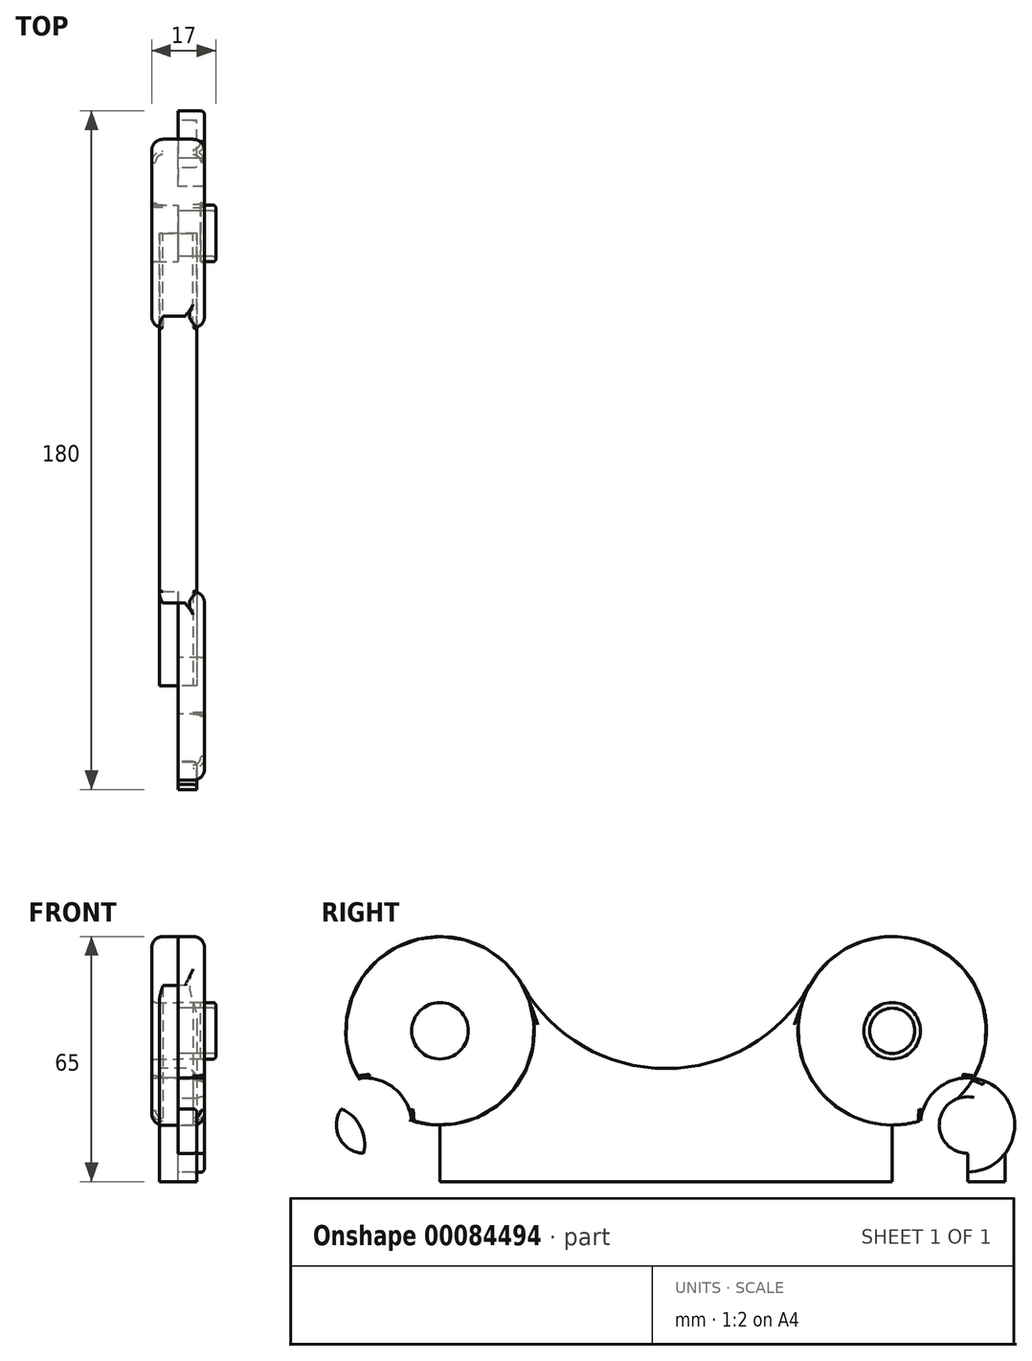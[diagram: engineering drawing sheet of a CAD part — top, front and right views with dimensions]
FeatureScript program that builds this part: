
annotation { "Feature Type Name" : "Feature", "Feature Type Description" : "" }
export const myFeature = defineFeature(function(context is Context, id is Id, definition is map)
    precondition{}
    {
        {
            var Q0;
            Q0=qCreatedBy(makeId("Right.planeOp"),FACE);
            var sketch = newSketch(context, id + "F0", { "sketchPlane" : qUnion([Q0])});
            skLineSegment(sketch, "E0.bottom", {"start": v(30, -20) * mm, "end": v(-30, -20) * mm});
            skLineSegment(sketch, "E0.top", {"start": v(30, 20) * mm, "end": v(-30, 20) * mm});
            skLineSegment(sketch, "E0.left", {"start": v(30, -20) * mm, "end": v(30, 20) * mm});
            skLineSegment(sketch, "E0.right", {"start": v(-30, -20) * mm, "end": v(-30, 20) * mm});
            skPoint(sketch, "E0.middle", {"position": v(0, 0) * mm});
            skCircle(sketch, "E1", {"center": v(30, 20) * mm, "radius": 25 * mm});
            skArc(sketch, "E2", {"start": v(-30, 10) * mm, "mid": v(-7.87, 15.98) * mm, "end": v(8.24, 32.3) * mm});
            skLineSegment(sketch, "E3", {"start": v(30, -20) * mm, "end": v(70, -20) * mm});
            skLineSegment(sketch, "E4", {"start": v(70, -20) * mm, "end": v(60, -20) * mm});
            skLineSegment(sketch, "E5", {"start": v(60, -20) * mm, "end": v(60, -10) * mm});
            skCircle(sketch, "E6", {"center": v(60, -10) * mm, "radius": 10 * mm});
            skLineSegment(sketch, "E7", {"start": v(69.11, -5.89) * mm, "end": v(52.79, 30.29) * mm});
            skLineSegment(sketch, "E8", {"start": v(60, -20) * mm, "end": v(50, -20) * mm});
            skLineSegment(sketch, "E9", {"start": v(50, -20) * mm, "end": v(50, -5) * mm});
            skCircle(sketch, "E10", {"center": v(50, -5) * mm, "radius": 7.5 * mm});
            skCircle(sketch, "E11.cCircle", {"center": v(50, -5) * mm, "radius": 7.5 * mm, "construction": true});
            skCircle(sketch, "E12", {"center": v(30, 20) * mm, "radius": 7.5 * mm});
            skCircle(sketch, "E13.cCircle", {"center": v(30, 20) * mm, "radius": 7.5 * mm, "construction": true});
            skCircle(sketch, "E14", {"center": v(50, -5) * mm, "radius": 12.5 * mm});
            skLineSegment(sketch, "E15", {"start": v(-30, 10) * mm, "end": v(30, 10) * mm});
            skCircle(sketch, "E16", {"center": v(30, 20) * mm, "radius": 6 * mm});
            skSolve(sketch);
        }
        {
            var Q0;
            {var subQ1=sQuery(id+"F0.wireOp",EDGE,"E0.bottom");Q0=makeQuery(id+"F0.imprint","IMPRINT",FACE,{"disambiguationData":[TD([[makeQuery(id+"F0.imprint","IMPRINT",EDGE,{"derivedFrom":subQ1}),-1.0]])]});}
            var Q1;
            {var subQ0=sQuery(id+"F0.wireOp",EDGE,"E13.2");Q1=makeQuery(id+"F0.imprint","IMPRINT",FACE,{"disambiguationData":[TD([[makeQuery(id+"F0.imprint","IMPRINT",EDGE,{"derivedFrom":subQ0}),-1.0]])]});}
            var Q2;
            {var subQ5=sQuery(id+"F0.wireOp",EDGE,"E13.0");Q2=makeQuery(id+"F0.imprint","IMPRINT",FACE,{"disambiguationData":[TD([[makeQuery(id+"F0.imprint","IMPRINT",EDGE,{"derivedFrom":subQ5}),-1.0]])]});}
            var Q3;
            {var subQ5=sQuery(id+"F0.wireOp",EDGE,"9949395a-d663-43b6-ab1f-91bd425a46a5.5");Q3=makeQuery(id+"F0.imprint","IMPRINT",FACE,{"disambiguationData":[TD([[makeQuery(id+"F0.imprint","IMPRINT",EDGE,{"derivedFrom":subQ5}),-1.0]])]});}
            var Q4;
            {var subQ3=sQuery(id+"F0.wireOp",EDGE,"9949395a-d663-43b6-ab1f-91bd425a46a5.0");Q4=makeQuery(id+"F0.imprint","IMPRINT",FACE,{"disambiguationData":[TD([[makeQuery(id+"F0.imprint","IMPRINT",EDGE,{"derivedFrom":subQ3}),-1.0]])]});}
            var Q5;
            {var subQ7=sQuery(id+"F0.wireOp",EDGE,"E3");Q5=makeQuery(id+"F0.imprint","IMPRINT",FACE,{"disambiguationData":[TD([[makeQuery(id+"F0.imprint","IMPRINT",EDGE,{"derivedFrom":subQ7}),1.0]])]});}
            var Q6;
            {var subQ7=sQuery(id+"F0.wireOp",EDGE,"RmBogFvs-hSfI-Fk4R-dt5A-n03ufGh0CfcG");Q6=makeQuery(id+"F0.imprint","IMPRINT",FACE,{"disambiguationData":[TD([[makeQuery(id+"F0.imprint","IMPRINT",EDGE,{"derivedFrom":subQ7}),-1.0]])]});}
            var Q7;
            {var subQ0=sQuery(id+"F0.wireOp",EDGE,"2t1OXQJq-y7Vc-evad-L2Xn-u0VWQIfUzRHt");var subQ1=makeQuery(id+"F0.imprint","INTERSECT",VERTEX,{"derivedFrom":[subQ0,sQuery(id+"F0.wireOp",EDGE,"sKefAVml-Ko5n-3xTP-831O-t11bm8OxiufM")]});Q7=makeQuery(id+"F0.imprint","IMPRINT",FACE,{"disambiguationData":[TD([[makeQuery(id+"F0.imprint","IMPRINT",EDGE,{"disambiguationData":[TD([[subQ1,1.0]])],"derivedFrom":subQ0}),1.0]])]});}
            var Q8;
            {var subQ5=sQuery(id+"F0.wireOp",EDGE,"bd8dee19-a407-44eb-8f93-f0fc487aa449.3");Q8=makeQuery(id+"F0.imprint","IMPRINT",FACE,{"disambiguationData":[TD([[makeQuery(id+"F0.imprint","IMPRINT",EDGE,{"derivedFrom":subQ5}),-1.0]])]});}
            var Q9;
            {var subQ0=sQuery(id+"F0.wireOp",EDGE,"bd8dee19-a407-44eb-8f93-f0fc487aa449.1");Q9=makeQuery(id+"F0.imprint","IMPRINT",FACE,{"disambiguationData":[TD([[makeQuery(id+"F0.imprint","IMPRINT",EDGE,{"derivedFrom":subQ0}),-1.0]])]});}
            var Q10;
            {var subQ0=sQuery(id+"F0.wireOp",EDGE,"E11.0");Q10=makeQuery(id+"F0.imprint","IMPRINT",FACE,{"disambiguationData":[TD([[makeQuery(id+"F0.imprint","IMPRINT",EDGE,{"derivedFrom":subQ0}),-1.0]])]});}
            var Q11;
            {var subQ0=sQuery(id+"F0.wireOp",EDGE,"E11.4");Q11=makeQuery(id+"F0.imprint","IMPRINT",FACE,{"disambiguationData":[TD([[makeQuery(id+"F0.imprint","IMPRINT",EDGE,{"derivedFrom":subQ0}),-1.0]])]});}
            var Q12;
            {var subQ0=sQuery(id+"F0.wireOp",EDGE,"46ax8Qey-YlKV-k2xy-i6VS-7Ej97oajGADz");var subQ1=sQuery(id+"F0.wireOp",EDGE,"2t1OXQJq-y7Vc-evad-L2Xn-u0VWQIfUzRHt");var subQ2=makeQuery(id+"F0.imprint","INTERSECT",VERTEX,{"derivedFrom":[subQ1,subQ0]});Q12=makeQuery(id+"F0.imprint","IMPRINT",FACE,{"disambiguationData":[TD([[makeQuery(id+"F0.imprint","IMPRINT",EDGE,{"disambiguationData":[TD([[subQ2,1.0]])],"derivedFrom":subQ1}),-1.0]])]});}
            var Q13;
            {var subQ0=sQuery(id+"F0.wireOp",EDGE,"3qyVSIB1-lFnq-SXgv-lqWt-4zmXsfzFFz89");Q13=makeQuery(id+"F0.imprint","IMPRINT",FACE,{"disambiguationData":[TD([[makeQuery(id+"F0.imprint","IMPRINT",EDGE,{"derivedFrom":subQ0}),1.0]])]});}
            var Q14;
            {var subQ0=sQuery(id+"F0.wireOp",EDGE,"E2");var subQ1=sQuery(id+"F0.wireOp",EDGE,"E0.top");var subQ2=makeQuery(id+"F0.imprint","INTERSECT",VERTEX,{"disambiguationData":[OD(1.0)],"derivedFrom":[subQ1,subQ0]});Q14=makeQuery(id+"F0.imprint","IMPRINT",FACE,{"disambiguationData":[TD([[makeQuery(id+"F0.imprint","IMPRINT",EDGE,{"disambiguationData":[TD([[subQ2,-1.0]])],"derivedFrom":subQ1}),-1.0]])]});}
            var Q15;
            {var subQ0=sQuery(id+"F0.wireOp",EDGE,"E2");var subQ1=sQuery(id+"F0.wireOp",EDGE,"E0.top");var subQ2=makeQuery(id+"F0.imprint","INTERSECT",VERTEX,{"disambiguationData":[OD(0.0)],"derivedFrom":[subQ1,subQ0]});Q15=makeQuery(id+"F0.imprint","IMPRINT",FACE,{"disambiguationData":[TD([[makeQuery(id+"F0.imprint","IMPRINT",EDGE,{"disambiguationData":[TD([[subQ2,1.0]])],"derivedFrom":subQ1}),-1.0]])]});}
            var Q16;
            {var subQ0=sQuery(id+"F0.wireOp",EDGE,"E6");var subQ1=makeQuery(id+"F0.imprint","INTERSECT",VERTEX,{"derivedFrom":[subQ0,sQuery(id+"F0.wireOp",EDGE,"E7")]});Q16=makeQuery(id+"F0.imprint","IMPRINT",FACE,{"disambiguationData":[TD([[makeQuery(id+"F0.imprint","IMPRINT",EDGE,{"disambiguationData":[TD([[subQ1,-1.0]])],"derivedFrom":subQ0}),1.0]])]});}
            var Q17;
            {var subQ0=sQuery(id+"F0.wireOp",EDGE,"E8");Q17=makeQuery(id+"F0.imprint","IMPRINT",FACE,{"disambiguationData":[TD([[makeQuery(id+"F0.imprint","IMPRINT",EDGE,{"derivedFrom":subQ0}),-1.0]])]});}
            var Q18;
            {var subQ0=sQuery(id+"F0.wireOp",EDGE,"E2");var subQ1=sQuery(id+"F0.wireOp",EDGE,"E0.top");var subQ2=makeQuery(id+"F0.imprint","INTERSECT",VERTEX,{"derivedFrom":[subQ1,subQ0]});Q18=makeQuery(id+"F0.imprint","IMPRINT",FACE,{"disambiguationData":[TD([[makeQuery(id+"F0.imprint","IMPRINT",EDGE,{"disambiguationData":[TD([[subQ2,1.0]])],"derivedFrom":subQ1}),1.0]])]});}
            var Q19;
            {var subQ1=sQuery(id+"F0.wireOp",EDGE,"E5");var subQ3=sQuery(id+"F0.wireOp",EDGE,"E14");var subQ4=makeQuery(id+"F0.imprint","INTERSECT",VERTEX,{"derivedFrom":[subQ1,subQ3]});Q19=makeQuery(id+"F0.imprint","IMPRINT",FACE,{"disambiguationData":[TD([[makeQuery(id+"F0.imprint","IMPRINT",EDGE,{"disambiguationData":[TD([[subQ4,1.0]])],"derivedFrom":subQ3}),-1.0]])]});}
            var Q20;
            {var subQ0=sQuery(id+"F0.wireOp",EDGE,"E7");Q20=makeQuery(id+"F0.imprint","IMPRINT",FACE,{"disambiguationData":[TD([[makeQuery(id+"F0.imprint","IMPRINT",EDGE,{"derivedFrom":subQ0}),1.0]])]});}
            extrude(context, id + "F1", {"entities" : qUnion([Q0, Q1, Q2, Q3, Q4, Q5, Q6, Q7, Q8, Q9, Q10, Q11, Q12, Q13, Q14, Q15, Q16, Q17, Q18, Q19, Q20]), "depth" : 5 * mm});
        }
        {
            var Q0;
            {var subQ5=sQuery(id+"F0.wireOp",EDGE,"E12");var subQ8=sQuery(id+"F0.wireOp",EDGE,"E0.top");var subQ9=makeQuery(id+"F0.imprint","INTERSECT",VERTEX,{"derivedFrom":[subQ8,subQ5]});Q0=makeQuery(id+"F0.imprint","IMPRINT",FACE,{"disambiguationData":[TD([[makeQuery(id+"F0.imprint","IMPRINT",EDGE,{"disambiguationData":[TD([[subQ9,-1.0]])],"derivedFrom":subQ8}),-1.0]])]});}
            var Q1;
            {var subQ1=sQuery(id+"F0.wireOp",EDGE,"E0.top");var subQ5=sQuery(id+"F0.wireOp",EDGE,"E12");var subQ6=makeQuery(id+"F0.imprint","INTERSECT",VERTEX,{"derivedFrom":[subQ1,subQ5]});Q1=makeQuery(id+"F0.imprint","IMPRINT",FACE,{"disambiguationData":[TD([[makeQuery(id+"F0.imprint","IMPRINT",EDGE,{"disambiguationData":[TD([[subQ6,-1.0]])],"derivedFrom":subQ1}),1.0]])]});}
            var Q2;
            {var subQ0=sQuery(id+"F0.wireOp",EDGE,"E15");var subQ1=sQuery(id+"F0.wireOp",EDGE,"E0.left");var subQ2=makeQuery(id+"F0.imprint","INTERSECT",VERTEX,{"derivedFrom":[subQ1,subQ0]});Q2=makeQuery(id+"F0.imprint","IMPRINT",FACE,{"disambiguationData":[TD([[makeQuery(id+"F0.imprint","IMPRINT",EDGE,{"disambiguationData":[TD([[subQ2,1.0]])],"derivedFrom":subQ1}),1.0]])]});}
            var Q3;
            {var subQ0=sQuery(id+"F0.wireOp",EDGE,"E14");var subQ1=sQuery(id+"F0.wireOp",EDGE,"E6");var subQ2=makeQuery(id+"F0.imprint","INTERSECT",VERTEX,{"disambiguationData":[OD(0.0)],"derivedFrom":[subQ1,subQ0]});Q3=makeQuery(id+"F0.imprint","IMPRINT",FACE,{"disambiguationData":[TD([[makeQuery(id+"F0.imprint","IMPRINT",EDGE,{"disambiguationData":[TD([[subQ2,-1.0]])],"derivedFrom":subQ1}),-1.0]])]});}
            var Q4;
            {var subQ0=sQuery(id+"F0.wireOp",EDGE,"E14");var subQ2=sQuery(id+"F0.wireOp",EDGE,"E6");var subQ7=makeQuery(id+"F0.imprint","INTERSECT",VERTEX,{"disambiguationData":[OD(0.0)],"derivedFrom":[subQ2,subQ0]});Q4=makeQuery(id+"F0.imprint","IMPRINT",FACE,{"disambiguationData":[TD([[makeQuery(id+"F0.imprint","IMPRINT",EDGE,{"disambiguationData":[TD([[subQ7,-1.0]])],"derivedFrom":subQ2}),1.0]])]});}
            var Q5;
            {var subQ0=sQuery(id+"F0.wireOp",EDGE,"E10");var subQ1=sQuery(id+"F0.wireOp",EDGE,"E6");var subQ2=makeQuery(id+"F0.imprint","INTERSECT",VERTEX,{"disambiguationData":[OD(1.0)],"derivedFrom":[subQ1,subQ0]});Q5=makeQuery(id+"F0.imprint","IMPRINT",FACE,{"disambiguationData":[TD([[makeQuery(id+"F0.imprint","IMPRINT",EDGE,{"disambiguationData":[TD([[subQ2,-1.0]])],"derivedFrom":subQ1}),-1.0]])]});}
            var Q6;
            {var subQ0=sQuery(id+"F0.wireOp",EDGE,"E14");var subQ1=sQuery(id+"F0.wireOp",EDGE,"E1");var subQ2=makeQuery(id+"F0.imprint","INTERSECT",VERTEX,{"disambiguationData":[OD(0.0)],"derivedFrom":[subQ1,subQ0]});Q6=makeQuery(id+"F0.imprint","IMPRINT",FACE,{"disambiguationData":[TD([[makeQuery(id+"F0.imprint","IMPRINT",EDGE,{"disambiguationData":[TD([[subQ2,-1.0]])],"derivedFrom":subQ1}),1.0]])]});}
            var Q7;
            {var subQ0=sQuery(id+"F0.wireOp",EDGE,"E14");var subQ1=sQuery(id+"F0.wireOp",EDGE,"E1");var subQ2=makeQuery(id+"F0.imprint","INTERSECT",VERTEX,{"disambiguationData":[OD(0.0)],"derivedFrom":[subQ1,subQ0]});Q7=makeQuery(id+"F0.imprint","IMPRINT",FACE,{"disambiguationData":[TD([[makeQuery(id+"F0.imprint","IMPRINT",EDGE,{"disambiguationData":[TD([[subQ2,-1.0]])],"derivedFrom":subQ1}),-1.0]])]});}
            var Q8;
            {var subQ0=sQuery(id+"F0.wireOp",EDGE,"E0.left");var subQ1=sQuery(id+"F0.wireOp",EDGE,"E0.top");var subQ2=makeQuery(id+"F0.imprint","INTERSECT",VERTEX,{"derivedFrom":[subQ1,subQ0]});Q8=makeQuery(id+"F0.imprint","IMPRINT",FACE,{"disambiguationData":[TD([[makeQuery(id+"F0.imprint","IMPRINT",EDGE,{"disambiguationData":[TD([[subQ2,-1.0]])],"derivedFrom":subQ1}),1.0]])]});}
            var Q9;
            {var subQ0=sQuery(id+"F0.wireOp",EDGE,"E0.left");var subQ1=sQuery(id+"F0.wireOp",EDGE,"E0.top");var subQ2=makeQuery(id+"F0.imprint","INTERSECT",VERTEX,{"derivedFrom":[subQ1,subQ0]});Q9=makeQuery(id+"F0.imprint","IMPRINT",FACE,{"disambiguationData":[TD([[makeQuery(id+"F0.imprint","IMPRINT",EDGE,{"disambiguationData":[TD([[subQ2,-1.0]])],"derivedFrom":subQ1}),-1.0]])]});}
            var Q10;
            {var subQ0=sQuery(id+"F0.wireOp",EDGE,"E10");var subQ1=sQuery(id+"F0.wireOp",EDGE,"E1");var subQ2=makeQuery(id+"F0.imprint","INTERSECT",VERTEX,{"disambiguationData":[OD(0.0)],"derivedFrom":[subQ1,subQ0]});Q10=makeQuery(id+"F0.imprint","IMPRINT",FACE,{"disambiguationData":[TD([[makeQuery(id+"F0.imprint","IMPRINT",EDGE,{"disambiguationData":[TD([[subQ2,-1.0]])],"derivedFrom":subQ1}),1.0]])]});}
            var Q11;
            {var subQ0=sQuery(id+"F0.wireOp",EDGE,"E10");var subQ1=sQuery(id+"F0.wireOp",EDGE,"E1");var subQ8=makeQuery(id+"F0.imprint","INTERSECT",VERTEX,{"disambiguationData":[OD(0.0)],"derivedFrom":[subQ1,subQ0]});Q11=makeQuery(id+"F0.imprint","IMPRINT",FACE,{"disambiguationData":[TD([[makeQuery(id+"F0.imprint","IMPRINT",EDGE,{"disambiguationData":[TD([[subQ8,-1.0]])],"derivedFrom":subQ1}),-1.0]])]});}
            var Q12;
            {var subQ0=sQuery(id+"F0.wireOp",EDGE,"E6");var subQ1=makeQuery(id+"F0.imprint","INTERSECT",VERTEX,{"derivedFrom":[subQ0,sQuery(id+"F0.wireOp",EDGE,"E9")]});Q12=makeQuery(id+"F0.imprint","IMPRINT",FACE,{"disambiguationData":[TD([[makeQuery(id+"F0.imprint","IMPRINT",EDGE,{"disambiguationData":[TD([[subQ1,1.0]])],"derivedFrom":subQ0}),1.0]])]});}
            var Q13;
            {var subQ0=sQuery(id+"F0.wireOp",EDGE,"E9");var subQ1=sQuery(id+"F0.wireOp",EDGE,"E6");var subQ2=makeQuery(id+"F0.imprint","INTERSECT",VERTEX,{"derivedFrom":[subQ1,subQ0]});Q13=makeQuery(id+"F0.imprint","IMPRINT",FACE,{"disambiguationData":[TD([[makeQuery(id+"F0.imprint","IMPRINT",EDGE,{"disambiguationData":[TD([[subQ2,-1.0]])],"derivedFrom":subQ1}),-1.0]])]});}
            extrude(context, id + "F2", {"entities" : qUnion([Q0, Q1, Q2, Q3, Q4, Q5, Q6, Q7, Q8, Q9, Q10, Q11, Q12, Q13]), "depth" : 7 * mm});
        }
        {
            var Q0;
            {var subQ0=sQuery(id+"F0.wireOp",EDGE,"E16");var subQ1=sQuery(id+"F0.wireOp",EDGE,"E0.top");var subQ2=makeQuery(id+"F0.imprint","INTERSECT",VERTEX,{"derivedFrom":[subQ1,subQ0]});Q0=makeQuery(id+"F0.imprint","IMPRINT",FACE,{"disambiguationData":[TD([[makeQuery(id+"F0.imprint","IMPRINT",EDGE,{"disambiguationData":[TD([[subQ2,-1.0]])],"derivedFrom":subQ1}),-1.0]])]});}
            var Q1;
            {var subQ0=sQuery(id+"F0.wireOp",EDGE,"E16");var subQ1=sQuery(id+"F0.wireOp",EDGE,"E0.top");var subQ2=makeQuery(id+"F0.imprint","INTERSECT",VERTEX,{"derivedFrom":[subQ1,subQ0]});Q1=makeQuery(id+"F0.imprint","IMPRINT",FACE,{"disambiguationData":[TD([[makeQuery(id+"F0.imprint","IMPRINT",EDGE,{"disambiguationData":[TD([[subQ2,-1.0]])],"derivedFrom":subQ1}),1.0]])]});}
            extrude(context, id + "F3", {"entities" : qUnion([Q0, Q1]), "depth" : 10 * mm});
        }
        {
            var Q0;
            Q0=makeQuery(id+"F3.opExtrude","CAP_EDGE",EDGE,{"disambiguationData":[OSD([sQuery(id+"F0.wireOp",EDGE,"E12")])],"isStart":false});
            var Q1;
            Q1=makeQuery(id+"F3.opExtrude","CAP_EDGE",EDGE,{"disambiguationData":[OSD([sQuery(id+"F0.wireOp",EDGE,"E16")])],"isStart":false});
            fillet(context, id + "F4", {"entities" : qUnion([Q0, Q1]), "radius" : 0.7 * mm, "tangentPropagation" : true, "allowEdgeOverflow" : false});
        }
        {
            var Q0;
            Q0=makeQuery(id+"F2.opExtrude","CAP_EDGE",EDGE,{"disambiguationData":[OSD([sQuery(id+"F0.wireOp",EDGE,"E1")])],"isStart":false});
            var Q1;
            Q1=makeQuery(id+"F10.opPattern","COPY",EDGE,{"derivedFrom":makeQuery(id+"F2.opExtrude","CAP_EDGE",EDGE,{"disambiguationData":[OSD([sQuery(id+"F0.wireOp",EDGE,"E1")])],"isStart":false}),"instanceName":"1"});
            fillet(context, id + "F5", {"entities" : qUnion([Q0, Q1]), "radius" : 3 * mm, "tangentPropagation" : true, "allowEdgeOverflow" : false});
        }
        {
            var Q0;
            Q0=makeQuery(id+"F2.opExtrude","CAP_EDGE",EDGE,{"disambiguationData":[OSD([sQuery(id+"F0.wireOp",EDGE,"E14")])],"isStart":false});
            fillet(context, id + "F6", {"entities" : qUnion([Q0]), "radius" : 1 * mm, "tangentPropagation" : true, "allowEdgeOverflow" : false});
        }
        {
            var Q0;
            {var subQ0=sQuery(id+"F0.wireOp",EDGE,"E1");var subQ1=makeQuery(id+"F0.imprint","INTERSECT",VERTEX,{"derivedFrom":[sQuery(id+"F0.wireOp",EDGE,"E0.left"),subQ0]});var subQ3=makeQuery(id+"F0.imprint","INTERSECT",VERTEX,{"derivedFrom":[sQuery(id+"F0.wireOp",EDGE,"E0.top"),subQ0]});Q0=makeQuery(id+"F1.opExtrude","CAP_EDGE",EDGE,{"disambiguationData":[OSD([subQ0]),TDD([makeQuery(id+"F0.imprint","IMPRINT",EDGE,{"disambiguationData":[TD([[makeQuery(id+"F0.imprint","INTERSECT",VERTEX,{"derivedFrom":[subQ0,sQuery(id+"F0.wireOp",EDGE,"E2")]}),-1.0]])],"derivedFrom":subQ0}),makeQuery(id+"F0.imprint","IMPRINT",EDGE,{"disambiguationData":[TD([[subQ3,-1.0]])],"derivedFrom":subQ0}),makeQuery(id+"F0.imprint","IMPRINT",EDGE,{"disambiguationData":[TD([[subQ1,1.0]])],"derivedFrom":subQ0}),makeQuery(id+"F0.imprint","IMPRINT",EDGE,{"disambiguationData":[TD([[subQ1,-1.0]])],"derivedFrom":subQ0})])],"isStart":false});}
            var Q1;
            {var subQ0=sQuery(id+"F0.wireOp",EDGE,"E1");Q1=makeQuery(id+"F1.opExtrude","CAP_EDGE",EDGE,{"disambiguationData":[OSD([subQ0]),TDD([makeQuery(id+"F0.imprint","IMPRINT",EDGE,{"disambiguationData":[TD([[makeQuery(id+"F0.imprint","INTERSECT",VERTEX,{"derivedFrom":[subQ0,sQuery(id+"F0.wireOp",EDGE,"E7")]}),1.0]])],"derivedFrom":subQ0})])],"isStart":false});}
            fillet(context, id + "F7", {"entities" : qUnion([Q0, Q1]), "radius" : 1 * mm, "tangentPropagation" : true, "allowEdgeOverflow" : false});
        }
        {
            var Q0;
            Q0=makeQuery(id+"F1.opExtrude","CAP_EDGE",EDGE,{"disambiguationData":[OSD([sQuery(id+"F0.wireOp",EDGE,"E14")])],"isStart":false});
            var Q1;
            Q1=makeQuery(id+"F2.opExtrude","CAP_EDGE",EDGE,{"disambiguationData":[OSD([sQuery(id+"F0.wireOp",EDGE,"E12")])],"isStart":false});
            fillet(context, id + "F8", {"entities" : qUnion([Q0, Q1]), "radius" : 1 * mm, "tangentPropagation" : true, "allowEdgeOverflow" : false});
        }
        {
            var Q0;
            Q0=makeQuery(id+"F1.opExtrude","CAP_EDGE",EDGE,{"disambiguationData":[OSD([sQuery(id+"F0.wireOp",EDGE,"E7")])],"isStart":false});
            var Q1;
            Q1=makeQuery(id+"F7.opFillet","BLEND_EDGE",EDGE,{"blendedFrom":[makeQuery(id+"F1.opExtrude","CAP_EDGE",EDGE,{"disambiguationData":[OSD([sQuery(id+"F0.wireOp",EDGE,"E1")])],"isStart":false}),makeQuery(id+"F1.opExtrude","SWEPT_FACE",FACE,{"disambiguationData":[OSD([sQuery(id+"F0.wireOp",EDGE,"E7")])]})],"blendedInto":[makeQuery(id+"F1.opExtrude","SWEPT_FACE",FACE,{"disambiguationData":[OSD([sQuery(id+"F0.wireOp",EDGE,"E7")])]})]});
            var Q2;
            Q2=makeQuery(id+"F1.opExtrude","CAP_EDGE",EDGE,{"disambiguationData":[OSD([sQuery(id+"F0.wireOp",EDGE,"E6")])],"isStart":false});
            fillet(context, id + "F9", {"entities" : qUnion([Q0, Q1, Q2]), "radius" : 1 * mm, "tangentPropagation" : true, "allowEdgeOverflow" : false});
        }
        {
            var Q0;
            Q0=makeQuery(id+"F1.opExtrude","SWEPT_BODY",BODY,{"disambiguationData":[OSD([sQuery(id+"F0.wireOp",EDGE,"E11.0"),sQuery(id+"F0.wireOp",EDGE,"E11.1"),sQuery(id+"F0.wireOp",EDGE,"E11.2"),sQuery(id+"F0.wireOp",EDGE,"E11.3"),sQuery(id+"F0.wireOp",EDGE,"E11.4"),sQuery(id+"F0.wireOp",EDGE,"E11.5")])]});
            var Q1;
            Q1=makeQuery(id+"F1.opExtrude","SWEPT_BODY",BODY,{"disambiguationData":[OSD([sQuery(id+"F0.wireOp",EDGE,"E13.0"),sQuery(id+"F0.wireOp",EDGE,"E13.1"),sQuery(id+"F0.wireOp",EDGE,"E13.2"),sQuery(id+"F0.wireOp",EDGE,"E13.3"),sQuery(id+"F0.wireOp",EDGE,"E13.4"),sQuery(id+"F0.wireOp",EDGE,"E13.5")])]});
            var Q2;
            Q2=makeQuery(id+"F2.opExtrude","SWEPT_BODY",BODY,{"disambiguationData":[OSD([sQuery(id+"F0.wireOp",EDGE,"E1"),sQuery(id+"F0.wireOp",EDGE,"E13.0"),sQuery(id+"F0.wireOp",EDGE,"E13.1"),sQuery(id+"F0.wireOp",EDGE,"E13.2"),sQuery(id+"F0.wireOp",EDGE,"E13.3"),sQuery(id+"F0.wireOp",EDGE,"E13.4"),sQuery(id+"F0.wireOp",EDGE,"E13.5")])]});
            var Q3;
            Q3=makeQuery(id+"F2.opExtrude","SWEPT_BODY",BODY,{"disambiguationData":[OSD([sQuery(id+"F0.wireOp",EDGE,"E11.0"),sQuery(id+"F0.wireOp",EDGE,"E11.1"),sQuery(id+"F0.wireOp",EDGE,"E11.2"),sQuery(id+"F0.wireOp",EDGE,"E11.3"),sQuery(id+"F0.wireOp",EDGE,"E11.4"),sQuery(id+"F0.wireOp",EDGE,"E11.5"),sQuery(id+"F0.wireOp",EDGE,"E14")])]});
            var Q4;
            Q4=makeQuery(id+"F1.opExtrude","SWEPT_BODY",BODY,{"disambiguationData":[OSD([sQuery(id+"F0.wireOp",EDGE,"E0.bottom"),sQuery(id+"F0.wireOp",EDGE,"E0.right"),sQuery(id+"F0.wireOp",EDGE,"E1"),sQuery(id+"F0.wireOp",EDGE,"E2"),sQuery(id+"F0.wireOp",EDGE,"E3"),sQuery(id+"F0.wireOp",EDGE,"E6"),sQuery(id+"F0.wireOp",EDGE,"E7"),sQuery(id+"F0.wireOp",EDGE,"E8"),sQuery(id+"F0.wireOp",EDGE,"E14")])]});
            var Q5;
            {var subQ6=sQuery(id+"F0.wireOp",EDGE,"E0.bottom");Q5=makeQuery(id+"F0.imprint","IMPRINT",FACE,{"disambiguationData":[TD([[makeQuery(id+"F0.imprint","IMPRINT",EDGE,{"derivedFrom":subQ6}),-1.0]])]});}
            mirror(context, id + "F10", {"entities" : qUnion([Q0, Q1, Q2, Q3, Q4]), "mirrorPlane" : qUnion([Q5])});
        }
        {
            var Q0;
            Q0=sQuery(id+"F0.wireOp",VERTEX,"E12.center");
            var Q1;
            Q1=sQuery(id+"F0.wireOp",VERTEX,"E14.center");
            var Q2;
            Q2=makeQuery(id+"F10.opPattern","COPY",BODY,{"derivedFrom":makeQuery(id+"F1.opExtrude","SWEPT_BODY",BODY,{"disambiguationData":[OSD([sQuery(id+"F0.wireOp",EDGE,"E0.bottom"),sQuery(id+"F0.wireOp",EDGE,"E0.right"),sQuery(id+"F0.wireOp",EDGE,"E1"),sQuery(id+"F0.wireOp",EDGE,"E2"),sQuery(id+"F0.wireOp",EDGE,"E3"),sQuery(id+"F0.wireOp",EDGE,"E6"),sQuery(id+"F0.wireOp",EDGE,"E7"),sQuery(id+"F0.wireOp",EDGE,"E8"),sQuery(id+"F0.wireOp",EDGE,"E14")])]}),"instanceName":"1"});
            var Q3;
            Q3=makeQuery(id+"F1.opExtrude","SWEPT_BODY",BODY,{"disambiguationData":[OSD([sQuery(id+"F0.wireOp",EDGE,"E0.bottom"),sQuery(id+"F0.wireOp",EDGE,"E0.right"),sQuery(id+"F0.wireOp",EDGE,"E1"),sQuery(id+"F0.wireOp",EDGE,"E2"),sQuery(id+"F0.wireOp",EDGE,"E3"),sQuery(id+"F0.wireOp",EDGE,"E6"),sQuery(id+"F0.wireOp",EDGE,"E7"),sQuery(id+"F0.wireOp",EDGE,"E8"),sQuery(id+"F0.wireOp",EDGE,"E14")])]});
            hole(context, id + "F11", {"style" : HoleStyle.SIMPLE, "endStyle" : HoleEndStyle.THROUGH, "oppositeDirection" : true, "standardTappedOrClearance" : lookupTablePath({ "standard" : "ISO", "size" : "7.8", "type" : "Drilled" }), "standardBlindInLast" : lookupTablePath({ "standard" : "ISO", "size" : "7.8", "type" : "Drilled" }), "holeDiameter" : 7.8 * mm, "locations" : qUnion([Q0, Q1]), "scope" : qUnion([Q2, Q3]), "isTappedThrough" : true});
        }
        {
            var Q0;
            Q0=makeQuery(id+"F1.opExtrude","SWEPT_BODY",BODY,{"disambiguationData":[OSD([sQuery(id+"F0.wireOp",EDGE,"E0.bottom"),sQuery(id+"F0.wireOp",EDGE,"E0.right"),sQuery(id+"F0.wireOp",EDGE,"E1"),sQuery(id+"F0.wireOp",EDGE,"E2"),sQuery(id+"F0.wireOp",EDGE,"E3"),sQuery(id+"F0.wireOp",EDGE,"E6"),sQuery(id+"F0.wireOp",EDGE,"E7"),sQuery(id+"F0.wireOp",EDGE,"E8"),sQuery(id+"F0.wireOp",EDGE,"E14")])]});
            var Q1;
            Q1=makeQuery(id+"F1.opExtrude","SWEPT_BODY",BODY,{"disambiguationData":[OSD([sQuery(id+"F0.wireOp",EDGE,"E11.0"),sQuery(id+"F0.wireOp",EDGE,"E11.1"),sQuery(id+"F0.wireOp",EDGE,"E11.2"),sQuery(id+"F0.wireOp",EDGE,"E11.3"),sQuery(id+"F0.wireOp",EDGE,"E11.4"),sQuery(id+"F0.wireOp",EDGE,"E11.5")])]});
            var Q2;
            Q2=makeQuery(id+"F1.opExtrude","SWEPT_BODY",BODY,{"disambiguationData":[OSD([sQuery(id+"F0.wireOp",EDGE,"E13.0"),sQuery(id+"F0.wireOp",EDGE,"E13.1"),sQuery(id+"F0.wireOp",EDGE,"E13.2"),sQuery(id+"F0.wireOp",EDGE,"E13.3"),sQuery(id+"F0.wireOp",EDGE,"E13.4"),sQuery(id+"F0.wireOp",EDGE,"E13.5")])]});
            var Q3;
            Q3=makeQuery(id+"F2.opExtrude","SWEPT_BODY",BODY,{"disambiguationData":[OSD([sQuery(id+"F0.wireOp",EDGE,"E1"),sQuery(id+"F0.wireOp",EDGE,"E13.0"),sQuery(id+"F0.wireOp",EDGE,"E13.1"),sQuery(id+"F0.wireOp",EDGE,"E13.2"),sQuery(id+"F0.wireOp",EDGE,"E13.3"),sQuery(id+"F0.wireOp",EDGE,"E13.4"),sQuery(id+"F0.wireOp",EDGE,"E13.5")])]});
            var Q4;
            Q4=makeQuery(id+"F2.opExtrude","SWEPT_BODY",BODY,{"disambiguationData":[OSD([sQuery(id+"F0.wireOp",EDGE,"E11.0"),sQuery(id+"F0.wireOp",EDGE,"E11.1"),sQuery(id+"F0.wireOp",EDGE,"E11.2"),sQuery(id+"F0.wireOp",EDGE,"E11.3"),sQuery(id+"F0.wireOp",EDGE,"E11.4"),sQuery(id+"F0.wireOp",EDGE,"E11.5"),sQuery(id+"F0.wireOp",EDGE,"E14")])]});
            var Q5;
            Q5=makeQuery(id+"F1.opExtrude","SWEPT_BODY",BODY,{"disambiguationData":[OSD([sQuery(id+"F0.wireOp",EDGE,"E10")])]});
            var Q6;
            Q6=makeQuery(id+"F10.opPattern","COPY",BODY,{"derivedFrom":makeQuery(id+"F1.opExtrude","SWEPT_BODY",BODY,{"disambiguationData":[OSD([sQuery(id+"F0.wireOp",EDGE,"E0.bottom"),sQuery(id+"F0.wireOp",EDGE,"E0.right"),sQuery(id+"F0.wireOp",EDGE,"E1"),sQuery(id+"F0.wireOp",EDGE,"E2"),sQuery(id+"F0.wireOp",EDGE,"E3"),sQuery(id+"F0.wireOp",EDGE,"E6"),sQuery(id+"F0.wireOp",EDGE,"E7"),sQuery(id+"F0.wireOp",EDGE,"E8"),sQuery(id+"F0.wireOp",EDGE,"E14")])]}),"instanceName":"1"});
            var Q7;
            Q7=makeQuery(id+"F1.opExtrude","SWEPT_FACE",FACE,{"disambiguationData":[OSD([sQuery(id+"F0.wireOp",EDGE,"E0.right")])]});
            mirror(context, id + "F12", {"operationType" : NewBodyOperationType.ADD, "entities" : qUnion([Q0, Q1, Q2, Q3, Q4, Q5, Q6]), "mirrorPlane" : qUnion([Q7])});
        }
        {
            var Q0;
            Q0=makeQuery(id+"F7.opFillet","BLEND_EDGE",EDGE,{"blendedFrom":[makeQuery(id+"F1.opExtrude","CAP_EDGE",EDGE,{"disambiguationData":[OSD([sQuery(id+"F0.wireOp",EDGE,"E1")])],"isStart":false}),makeQuery(id+"F1.opExtrude","SWEPT_FACE",FACE,{"disambiguationData":[OSD([sQuery(id+"F0.wireOp",EDGE,"E2")])]})],"blendedInto":[makeQuery(id+"F1.opExtrude","SWEPT_FACE",FACE,{"disambiguationData":[OSD([sQuery(id+"F0.wireOp",EDGE,"E2")])]})]});
            var Q1;
            {var subQ0=makeQuery(id+"F1.opExtrude","CAP_EDGE",EDGE,{"disambiguationData":[OSD([sQuery(id+"F0.wireOp",EDGE,"E2")])],"isStart":false});Q1=makeQuery(id+"F12.boolean.opBoolean","MERGE",EDGE,{"derivedFrom":[subQ0,makeQuery(id+"F12.opPattern","COPY",EDGE,{"derivedFrom":subQ0,"instanceName":"1"})]});}
            fillet(context, id + "F13", {"entities" : qUnion([Q0, Q1]), "radius" : 3 * mm, "tangentPropagation" : true, "allowEdgeOverflow" : false});
        }
    });
